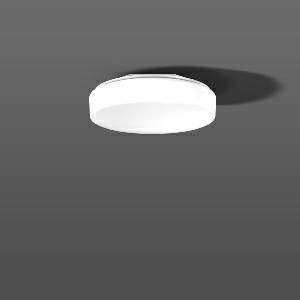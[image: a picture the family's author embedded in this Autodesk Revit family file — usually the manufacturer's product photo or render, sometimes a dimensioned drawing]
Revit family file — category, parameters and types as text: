
# Revit family: flat_polymero_kreis_672092_002_5_1_19_2968
name_source: partatom
category: Lighting Fixtures
units: mm (PartAtom-declared; Revit-internal decimal feet)

## family parameters
Cut with Voids When Loaded = No
Host = Face
Light Source = No
Part Type = Normal
Room Calculation Point = No
Round Connector Dimension = Use Diameter
Shared = No

## types (1)
- FLAT POLYMERO KREIS (1 x LED Modul 840, 1750 lm, 4000)
    Apparent Load = 15 VA
    CIE Flux Codes = 41 71 90 82 100
    Color Rendering = 80
    Color Temperature = 4000
    Default Elevation = 1800 mm
    Description = Series: FLAT POLYMERO KREIS
Decorative round surface-mounted luminaire. For escape route illumination. Base: metal, powder-coated. Diffuser made of non-yellowing plastic (PMMA), opal. Diffuser fastening: patented push system. Suitable for Ceiling mounting, Wall (surface). Functional parameters of the motion detector (ceiling mounting up to 4.0 m or wall mounting up to 2.7 m): HF detector 5.8 GHz ISM frequency band. Sensitivity/Range: 1-8 m in diameter, adjustable from 20-100%. Time control between 10 seconds and 30 minutes, adjustable. Coverage: 120°. Can be used as master luminaire up to 800 W (ohmic load), 500 W (fluorescent lamp, LED) / 400 A, 200 µs. Suitable for outdoor use to a limited extent only, as it is sensitive to all movements. 
Colour: white
Diameter: 360 mm
Height: 109 mm
Weight: 2.02 kg
Operating mode: Combined NL readiness
Duration time: 3 h
Lamp: LED
Socket: without socket
Colour temperature: 4000K
Colour rendering index (CRI): 80
System power: 15 W
Rated luminous flux: 1750 lm
Luminous flux, emergency: 200 lm
System power, emergency: -
Control gear: Regulated power supply
Protection class: I
Type of protection: IP 40
    Height = 109 mm
    Lamp = 1 x LED Modul 840
    Lamp Light Flux = 1750 lm
    Lamp count = 1
    Length = 360 mm
    Lifetime = 50000 h
    Luminous efficacy = 117 lm/W
    Manufacturer = RZB
    ModVariant = No
    Model = 672092.002.5.1.19
    Mounting Place = Ceiling
    Mounting Type = Surface mounted
    Number of Poles = 1
    OnlyDefault = Yes
    Power Factor = 1
    Product Name = FLAT POLYMERO KREIS
    Product group = Surface mounted ceiling and wall luminaires
    ProductGroupID = 305
    Protection Class = Protection class I
    Protection Degree = Degree of protection
    RLX_Detail_Level = 1
    RLX_Emergency_Light_Flux = 200 lm
    RLX_Emergency_Type = 3
    RLX_Emergency_Type_DB = Yes
    RlxData = <blob elided: 52405 chars, md5=6be7d2b6>
    Socket = socket
    Standby Power = 0 W
    System Light Flux = 1750 lm
    System Power = 15 W
    Type Comments = Product without accessories
    Type Image = 672092.002.1.jpg
    URL = http://relux.com
    VarID = ---
    Voltage = 0 V
    Weight = 0.00 kg
    Width = 0 mm  [stored 0 ft]

note: [stored X ft] marks values corroborated as IEEE doubles in the binary element streams (Revit-internal decimal feet)

## geometry (parser evidence)
native form markers: Blend x4, Sweep x11
no freeform markers — native parametric forms only
